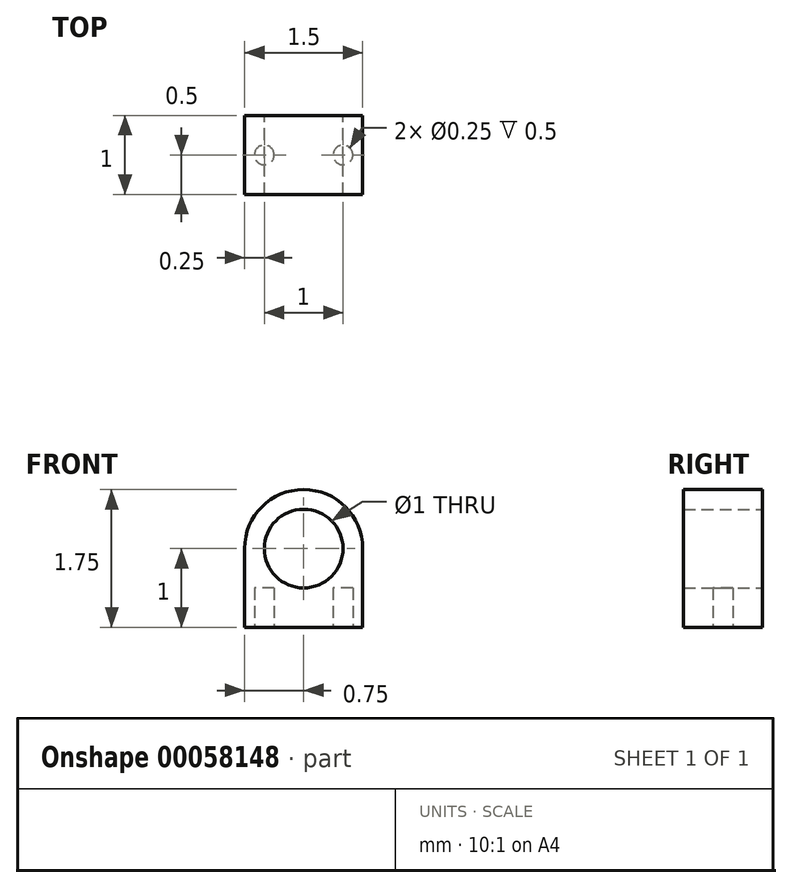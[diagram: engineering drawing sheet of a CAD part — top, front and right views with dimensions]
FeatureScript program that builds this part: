
annotation { "Feature Type Name" : "Feature", "Feature Type Description" : "" }
export const myFeature = defineFeature(function(context is Context, id is Id, definition is map)
    precondition{}
    {
        {
            var Q0;
            Q0=qCreatedBy(makeId("Front.planeOp"),FACE);
            var sketch = newSketch(context, id + "F0", { "sketchPlane" : qUnion([Q0])});
            skLineSegment(sketch, "E0", {"start": v(0, 0) * mm, "end": v(-0.75, 0) * mm});
            skLineSegment(sketch, "E1", {"start": v(-0.75, 0) * mm, "end": v(-0.75, 1) * mm});
            skArc(sketch, "E2", {"start": v(-0.75, 1) * mm, "mid": v(-0.53, 1.53) * mm, "end": v(0, 1.75) * mm});
            skCircle(sketch, "E3", {"center": v(0, 1) * mm, "radius": 0.5 * mm});
            skLineSegment(sketch, "E4.MirrorCS", {"start": v(0.75, 0) * mm, "end": v(0.75, 1) * mm});
            skLineSegment(sketch, "E5.MirrorCS", {"start": v(0, 0) * mm, "end": v(0.75, 0) * mm});
            skArc(sketch, "E6.MirrorCS", {"start": v(0.75, 1) * mm, "mid": v(0.53, 1.53) * mm, "end": v(0, 1.75) * mm});
            skSolve(sketch);
        }
        {
            var Q0;
            Q0 = qSketchRegion(id + "F0", true);
            var Q1;
            Q1=makeQuery(id+"F0.imprint","IMPRINT",FACE,{"disambiguationData":[TD([[makeQuery(id+"F0.imprint","IMPRINT",EDGE,{"derivedFrom":sQuery(id+"F0.wireOp",EDGE,"E0")}),-1.0]])]});
            extrude(context, id + "F1", {"entities" : qUnion([Q0, Q1]), "endBound" : BoundingType.SYMMETRIC, "depth" : 1 * mm});
        }
        {
            var Q0;
            Q0=qCreatedBy(makeId("Top.planeOp"),FACE);
            var sketch = newSketch(context, id + "F2", { "sketchPlane" : qUnion([Q0])});
            skCircle(sketch, "E7", {"center": v(-0.5, 0) * mm, "radius": 0.12 * mm});
            skCircle(sketch, "E8", {"center": v(0.5, 0) * mm, "radius": 0.12 * mm});
            skSolve(sketch);
        }
        {
            var Q0;
            Q0 = qSketchRegion(id + "F2", true);
            extrude(context, id + "F3", {"entities" : qUnion([Q0]), "operationType" : NewBodyOperationType.REMOVE, "depth" : 0.5 * mm});
        }
    });
